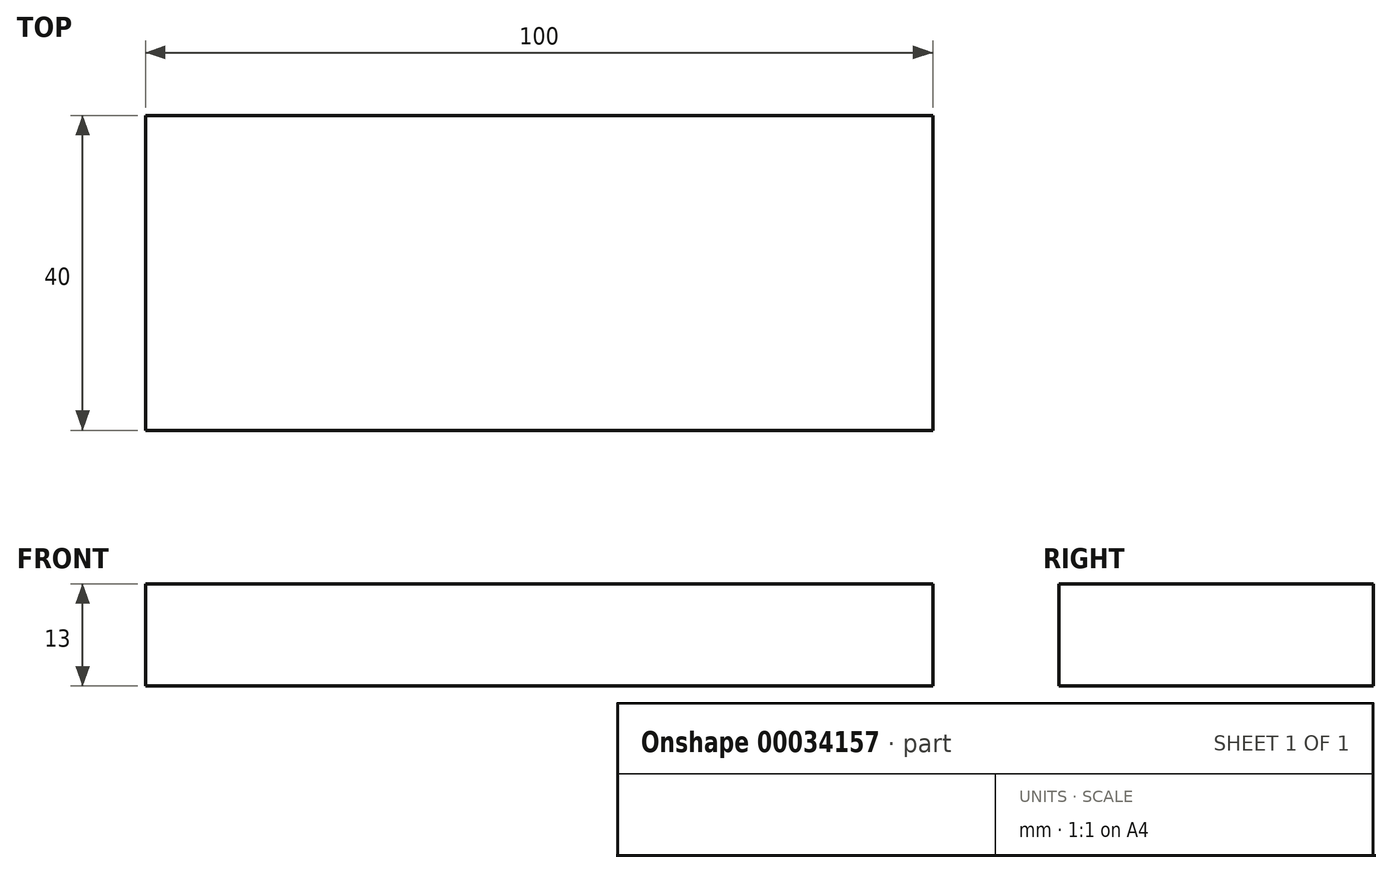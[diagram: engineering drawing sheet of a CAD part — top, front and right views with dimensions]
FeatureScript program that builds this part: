
annotation { "Feature Type Name" : "Feature", "Feature Type Description" : "" }
export const myFeature = defineFeature(function(context is Context, id is Id, definition is map)
    precondition{}
    {
        {
            var Q0;
            Q0=qCreatedBy(makeId("Top.planeOp"),FACE);
            var sketch = newSketch(context, id + "F0", { "sketchPlane" : qUnion([Q0])});
            skLineSegment(sketch, "E0.bottom", {"start": v(0, 0) * mm, "end": v(100, 0) * mm});
            skLineSegment(sketch, "E0.top", {"start": v(0, 40) * mm, "end": v(100, 40) * mm});
            skLineSegment(sketch, "E0.left", {"start": v(0, 0) * mm, "end": v(0, 40) * mm});
            skLineSegment(sketch, "E0.right", {"start": v(100, 0) * mm, "end": v(100, 40) * mm});
            skSolve(sketch);
        }
        {
            var Q0;
            Q0 = qSketchRegion(id + "F0", true);
            extrude(context, id + "F1", {"entities" : qUnion([Q0]), "depth" : 13 * mm});
        }
        {
            var Q0;
            Q0=makeQuery(id+"F1.opExtrude","SWEPT_FACE",FACE,{"disambiguationData":[OSD([sQuery(id+"F0.wireOp",EDGE,"E0.bottom")])]});
            var sketch = newSketch(context, id + "F2", { "sketchPlane" : qUnion([Q0])});
            skLineSegment(sketch, "E1.bottom", {"start": v(0, 5.4) * mm, "end": v(100, 5.4) * mm});
            skLineSegment(sketch, "E1.top", {"start": v(0, 2.97) * mm, "end": v(100, 2.97) * mm});
            skLineSegment(sketch, "E1.left", {"start": v(0, 5.4) * mm, "end": v(0, 2.97) * mm});
            skLineSegment(sketch, "E1.right", {"start": v(100, 5.4) * mm, "end": v(100, 2.97) * mm});
            skSolve(sketch);
        }
        {
            var Q0;
            Q0=makeQuery(id+"F2.imprint","IMPRINT",FACE,{"disambiguationData":[TD([[makeQuery(id+"F2.imprint","IMPRINT",EDGE,{"derivedFrom":sQuery(id+"F2.wireOp",EDGE,"E1.bottom")}),-1.0]])]});
            extrude(context, id + "F3", {"entities" : qUnion([Q0]), "operationType" : NewBodyOperationType.ADD, "oppositeDirection" : true, "depth" : 3 * mm});
        }
    });
